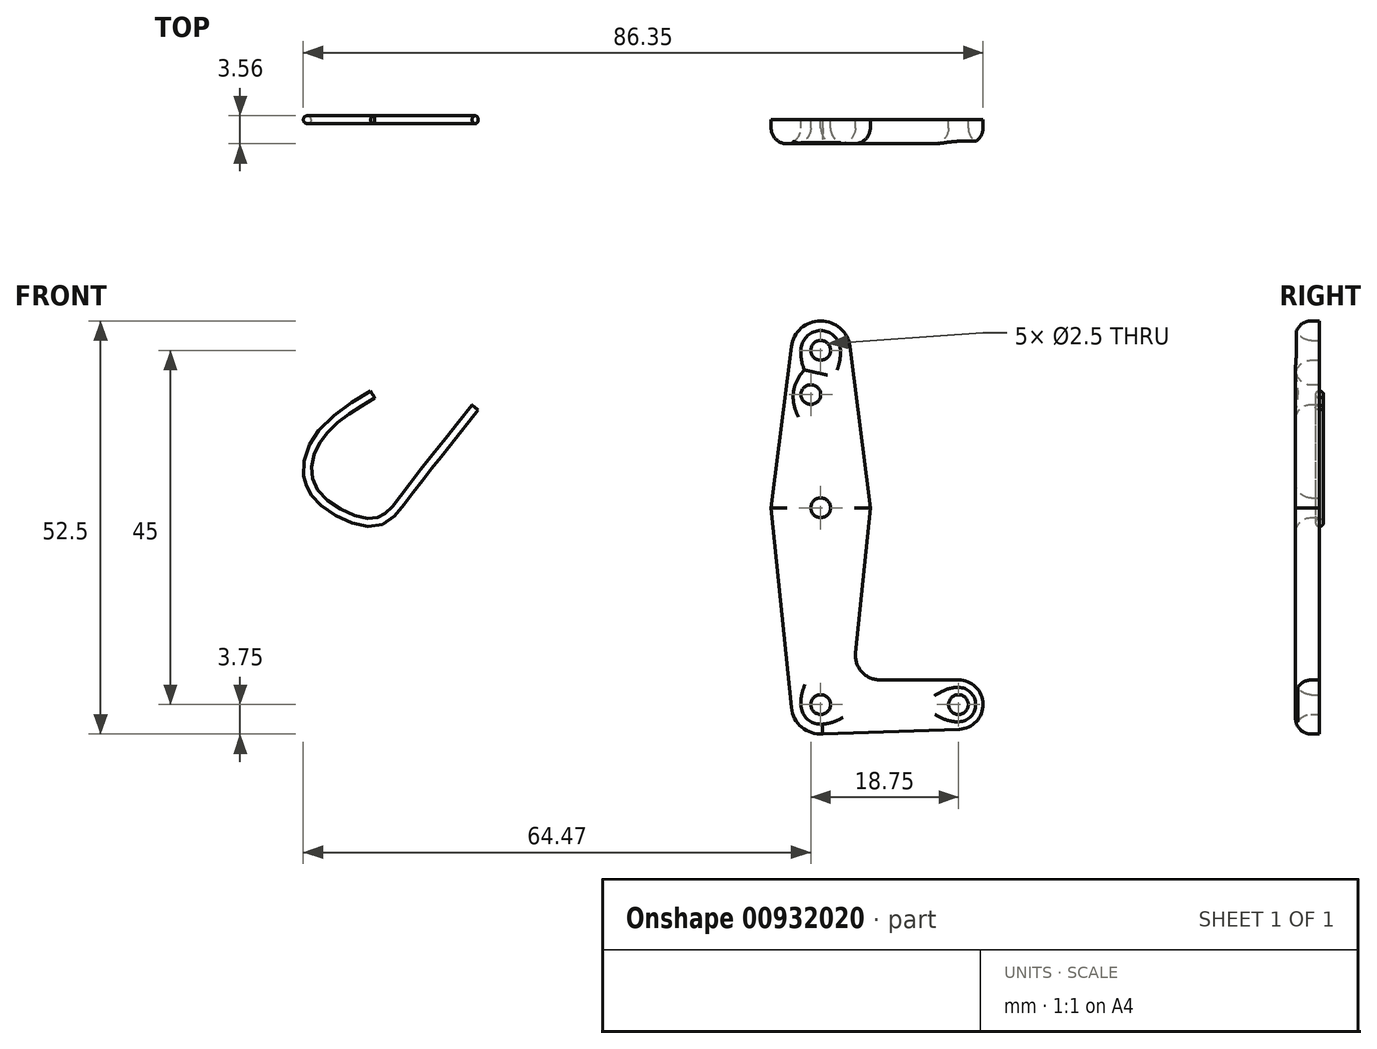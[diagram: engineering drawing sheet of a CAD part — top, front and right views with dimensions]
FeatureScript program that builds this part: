
annotation { "Feature Type Name" : "Feature", "Feature Type Description" : "" }
export const myFeature = defineFeature(function(context is Context, id is Id, definition is map)
    precondition{}
    {
        {
            var Q0;
            Q0=qCreatedBy(makeId("Front.planeOp"),FACE);
            var sketch = newSketch(context, id + "F0", { "sketchPlane" : qUnion([Q0])});
            skCircle(sketch, "E0", {"center": v(0, 0) * mm, "radius": 6.25 * mm});
            skCircle(sketch, "E1", {"center": v(0, -25) * mm, "radius": 3.75 * mm});
            skCircle(sketch, "E2", {"center": v(17.5, -25) * mm, "radius": 3.12 * mm});
            skCircle(sketch, "E3", {"center": v(0, 20) * mm, "radius": 3.75 * mm});
            skCircle(sketch, "E4", {"center": v(0, 20) * mm, "radius": 1.25 * mm});
            skCircle(sketch, "E5", {"center": v(0, 0) * mm, "radius": 1.25 * mm});
            skCircle(sketch, "E6", {"center": v(0, -25) * mm, "radius": 1.25 * mm});
            skCircle(sketch, "E7", {"center": v(17.5, -25) * mm, "radius": 1.25 * mm});
            skLineSegment(sketch, "E8", {"start": v(-3.72, 20.47) * mm, "end": v(-6.3, 0) * mm});
            skLineSegment(sketch, "E9", {"start": v(3.72, 20.47) * mm, "end": v(6.3, 0) * mm});
            skLineSegment(sketch, "E10", {"start": v(0, -28.75) * mm, "end": v(17.61, -28.12) * mm});
            skPoint(sketch, "E11.visualSharp", {"position": v(6.3, -17.39) * mm});
            skCircle(sketch, "E12", {"center": v(-1.25, 14.38) * mm, "radius": 1.25 * mm});
            skLineSegment(sketch, "E13", {"start": v(0, 15.68) * mm, "end": v(0, -18.6) * mm, "construction": true});
            skLineSegment(sketch, "E14", {"start": v(0, -25) * mm, "end": v(17.5, -25) * mm, "construction": true});
            skLineSegment(sketch, "E15", {"start": v(-6.3, 0) * mm, "end": v(-3.73, -25.38) * mm});
            skLineSegment(sketch, "E16", {"start": v(6.3, 0) * mm, "end": v(4.43, -18.43) * mm});
            skLineSegment(sketch, "E17", {"start": v(17.5, -21.87) * mm, "end": v(7.55, -21.87) * mm});
            skArc(sketch, "E18.filletArc", {"start": v(4.43, -18.43) * mm, "mid": v(5.23, -20.84) * mm, "end": v(7.55, -21.88) * mm});
            skFitSpline(sketch, "E19", {"points": [v(-43.9, 12.74) * mm, v(-53.1, 1.06) * mm, v(-56.9, -1.86) * mm, v(-64.53, 2.33) * mm, v(-63.77, 9) * mm, v(-56.9, 14.4) * mm], "startDerivative": vector(-39.56, -49.6) * mm, "endDerivative": vector(38.8, 23.05) * mm});
            skSolve(sketch);
        }
        {
            var Q0;
            Q0 = qSketchRegion(id + "F0", true);
            extrude(context, id + "F1", {"entities" : qUnion([Q0]), "depth" : 3.05 * mm, "offsetDistance" : 25 * mm});
        }
        {
            var Q0;
            Q0=sQuery(id+"F0.wireOp",VERTEX,"E19.start");
            var Q1;
            Q1=sQuery(id+"F0.wireOp",EDGE,"E19");
            cPlane(context, id + "F2", {"entities" : qUnion([Q0, Q1]), "cplaneType" : CPlaneType.CURVE_POINT, "offset" : 25 * mm, "width" : 150 * mm, "height" : 150 * mm});
        }
        {
            var Q0;
            Q0=qCreatedBy(id+"F2.planeOp",FACE);
            var sketch = newSketch(context, id + "F3", { "sketchPlane" : qUnion([Q0])});
            skCircle(sketch, "E20", {"center": v(-42.26, 0) * mm, "radius": 0.5 * mm});
            skSolve(sketch);
        }
        {
            var Q0;
            Q0=makeQuery(id+"F3.imprint","IMPRINT",FACE,{"disambiguationData":[TD([[makeQuery(id+"F3.imprint","IMPRINT",EDGE,{"derivedFrom":sQuery(id+"F3.wireOp",EDGE,"E20")}),1.0]])]});
            var Q1;
            Q1=sQuery(id+"F0.wireOp",EDGE,"E19");
            sweep(context, id + "F4", {"profiles" : qUnion([Q0]), "path" : qUnion([Q1])});
        }
        {
            var Q0;
            Q0=makeQuery(id+"F1.opExtrude","CAP_FACE",FACE,{"disambiguationData":[OSD([sQuery(id+"F0.wireOp",EDGE,"E1"),sQuery(id+"F0.wireOp",EDGE,"E2"),sQuery(id+"F0.wireOp",EDGE,"E3"),sQuery(id+"F0.wireOp",EDGE,"E4"),sQuery(id+"F0.wireOp",EDGE,"E5"),sQuery(id+"F0.wireOp",EDGE,"E6"),sQuery(id+"F0.wireOp",EDGE,"E7"),sQuery(id+"F0.wireOp",EDGE,"E8"),sQuery(id+"F0.wireOp",EDGE,"E9"),sQuery(id+"F0.wireOp",EDGE,"E10"),sQuery(id+"F0.wireOp",EDGE,"E12"),sQuery(id+"F0.wireOp",EDGE,"E15"),sQuery(id+"F0.wireOp",EDGE,"E16"),sQuery(id+"F0.wireOp",EDGE,"E17"),sQuery(id+"F0.wireOp",EDGE,"E18.filletArc")])],"isStart":false});
            fillet(context, id + "F5", {"entities" : qUnion([Q0]), "radius" : 2 * mm, "tangentPropagation" : true, "allowEdgeOverflow" : false});
        }
    });
